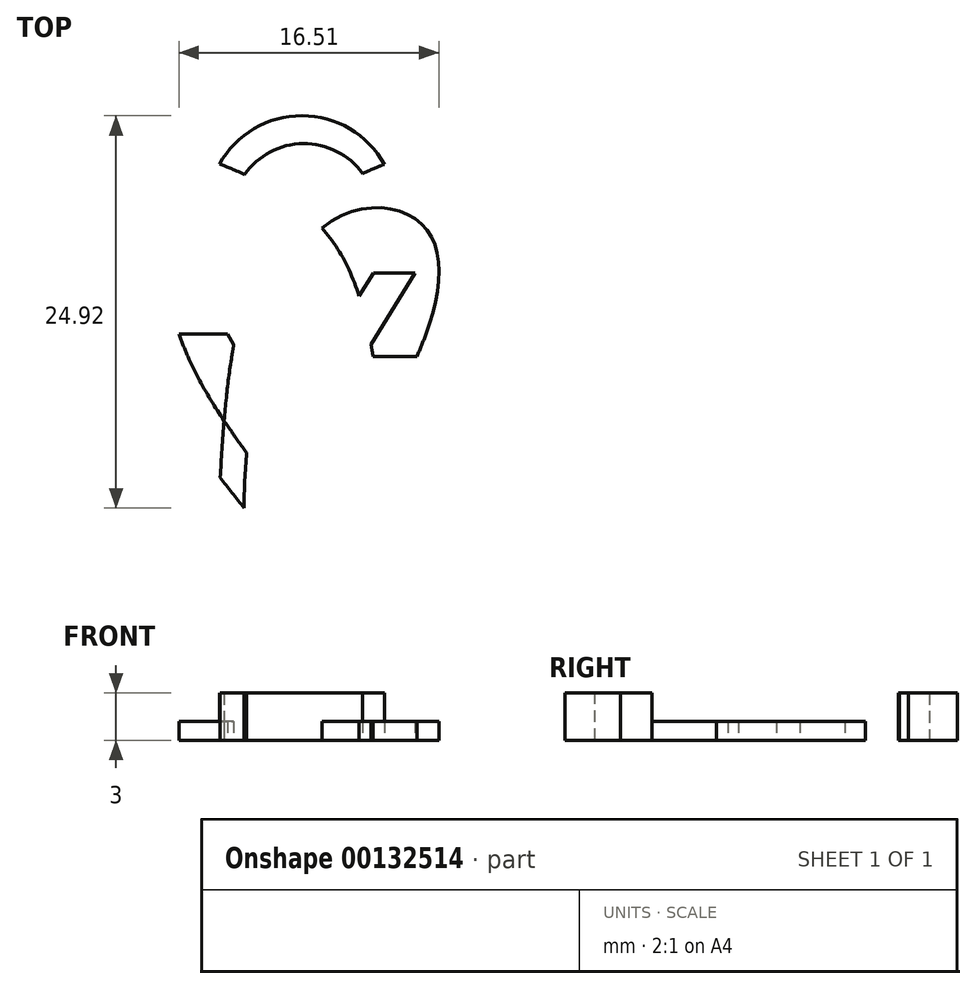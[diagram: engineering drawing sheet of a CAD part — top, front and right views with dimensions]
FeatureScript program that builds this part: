
annotation { "Feature Type Name" : "Feature", "Feature Type Description" : "" }
export const myFeature = defineFeature(function(context is Context, id is Id, definition is map)
    precondition{}
    {
        {
            var Q0;
            Q0=qCreatedBy(makeId("Top.planeOp"),FACE);
            var sketch = newSketch(context, id + "F0", { "sketchPlane" : qUnion([Q0])});
            skFitSpline(sketch, "E0", {"points": [v(0, -5.13) * mm, v(-6.3, 4.4) * mm, v(-7.94, 14.36) * mm, v(0, 13.22) * mm, v(2.94, -10.07) * mm, v(0, -5.13) * mm]});
            skFitSpline(sketch, "E1.MirrorCS", {"points": [v(0, -5.13) * mm, v(6.3, 4.4) * mm, v(7.94, 14.36) * mm, v(0, 13.22) * mm, v(-2.94, -10.07) * mm, v(0, -5.13) * mm]});
            skFitSpline(sketch, "E2", {"points": [v(0, -8.39) * mm, v(-10.5, 7.58) * mm, v(-9.2, 18.45) * mm, v(-5.18, 18.54) * mm, v(-5.05, 18.5) * mm, v(0, 15.7) * mm, v(4.4, 6.92) * mm, v(5.53, -11.48) * mm, v(5.2, -17.18) * mm, v(0, -8.39) * mm]});
            skFitSpline(sketch, "E3.MirrorCS", {"points": [v(0, -8.39) * mm, v(10.5, 7.58) * mm, v(9.2, 18.45) * mm, v(5.18, 18.54) * mm, v(5.05, 18.5) * mm, v(0, 15.7) * mm, v(-4.4, 6.92) * mm, v(-5.53, -11.48) * mm, v(-5.2, -17.18) * mm, v(0, -8.39) * mm]});
            skLineSegment(sketch, "E4", {"start": v(0, 0) * mm, "end": v(7.15, 11.64) * mm});
            skLineSegment(sketch, "E5", {"start": v(7.15, 11.64) * mm, "end": v(4.5, 11.64) * mm});
            skLineSegment(sketch, "E6", {"start": v(4.5, 11.64) * mm, "end": v(0, 4.3) * mm});
            skLineSegment(sketch, "E7.MirrorCS", {"start": v(-4.5, 11.64) * mm, "end": v(0, 4.3) * mm});
            skLineSegment(sketch, "E8.MirrorCS", {"start": v(-7.15, 11.64) * mm, "end": v(-4.5, 11.64) * mm});
            skLineSegment(sketch, "E9.MirrorCS", {"start": v(0, 0) * mm, "end": v(-7.15, 11.64) * mm});
            skPoint(sketch, "E10", {"position": v(0, 5.36) * mm});
            skLineSegment(sketch, "E11", {"start": v(-7.84, 7.76) * mm, "end": v(-4.77, 7.76) * mm});
            skLineSegment(sketch, "E12", {"start": v(-7.27, 6.35) * mm, "end": v(-3.9, 6.35) * mm});
            skLineSegment(sketch, "E13.MirrorCS", {"start": v(7.84, 7.76) * mm, "end": v(4.77, 7.76) * mm});
            skLineSegment(sketch, "E14.MirrorCS", {"start": v(7.27, 6.35) * mm, "end": v(3.9, 6.35) * mm});
            skArc(sketch, "E15", {"start": v(3.82, 17.97) * mm, "mid": v(0.05, 19.87) * mm, "end": v(-3.68, 17.9) * mm});
            skArc(sketch, "E16", {"start": v(5.2, 18.55) * mm, "mid": v(-0.03, 21.64) * mm, "end": v(-5.27, 18.56) * mm});
            skPoint(sketch, "E17.startSnap0", {"position": v(-0.03, 21.64) * mm});
            skLineSegment(sketch, "E18", {"start": v(-0.03, 21.64) * mm, "end": v(16.3, 21.61) * mm, "construction": true});
            skLineSegment(sketch, "E19", {"start": v(0, -8.39) * mm, "end": v(16.3, -8.39) * mm, "construction": true});
            skLineSegment(sketch, "E20", {"start": v(16.3, -8.39) * mm, "end": v(16.3, 21.61) * mm, "construction": true});
            skSolve(sketch);
        }
        {
            var Q0;
            {var subQ5=sQuery(id+"F0.wireOp",EDGE,"E1.MirrorCS");var subQ6=sQuery(id+"F0.wireOp",EDGE,"E0");var subQ7=makeQuery(id+"F0.imprint","INTERSECT",VERTEX,{"disambiguationData":[OD(0.0)],"derivedFrom":[subQ6,subQ5]});Q0=makeQuery(id+"F0.imprint","IMPRINT",FACE,{"disambiguationData":[TD([[makeQuery(id+"F0.imprint","IMPRINT",EDGE,{"disambiguationData":[TD([[subQ7,-1.0]])],"derivedFrom":subQ6}),1.0]])]});}
            var Q1;
            {var subQ0=sQuery(id+"F0.wireOp",EDGE,"E15");Q1=makeQuery(id+"F0.imprint","IMPRINT",FACE,{"disambiguationData":[TD([[makeQuery(id+"F0.imprint","IMPRINT",EDGE,{"derivedFrom":subQ0}),-1.0]])]});}
            extrude(context, id + "F1", {"entities" : qUnion([Q0, Q1]), "depth" : 3 * mm});
        }
        {
            var Q0;
            {var subQ0=sQuery(id+"F0.wireOp",EDGE,"E5");Q0=makeQuery(id+"F0.imprint","IMPRINT",FACE,{"disambiguationData":[TD([[makeQuery(id+"F0.imprint","IMPRINT",EDGE,{"derivedFrom":subQ0}),-1.0]])]});}
            var Q1;
            {var subQ3=sQuery(id+"F0.wireOp",EDGE,"E12");Q1=makeQuery(id+"F0.imprint","IMPRINT",FACE,{"disambiguationData":[TD([[makeQuery(id+"F0.imprint","IMPRINT",EDGE,{"derivedFrom":subQ3}),-1.0]])]});}
            var Q2;
            {var subQ0=sQuery(id+"F0.wireOp",EDGE,"E11");Q2=makeQuery(id+"F0.imprint","IMPRINT",FACE,{"disambiguationData":[TD([[makeQuery(id+"F0.imprint","IMPRINT",EDGE,{"derivedFrom":subQ0}),-1.0]])]});}
            var Q3;
            {var subQ0=sQuery(id+"F0.wireOp",EDGE,"E13.MirrorCS");Q3=makeQuery(id+"F0.imprint","IMPRINT",FACE,{"disambiguationData":[TD([[makeQuery(id+"F0.imprint","IMPRINT",EDGE,{"derivedFrom":subQ0}),1.0]])]});}
            extrude(context, id + "F2", {"entities" : qUnion([Q0, Q1, Q2, Q3]), "operationType" : NewBodyOperationType.ADD, "depth" : 1.2 * mm});
        }
    });
